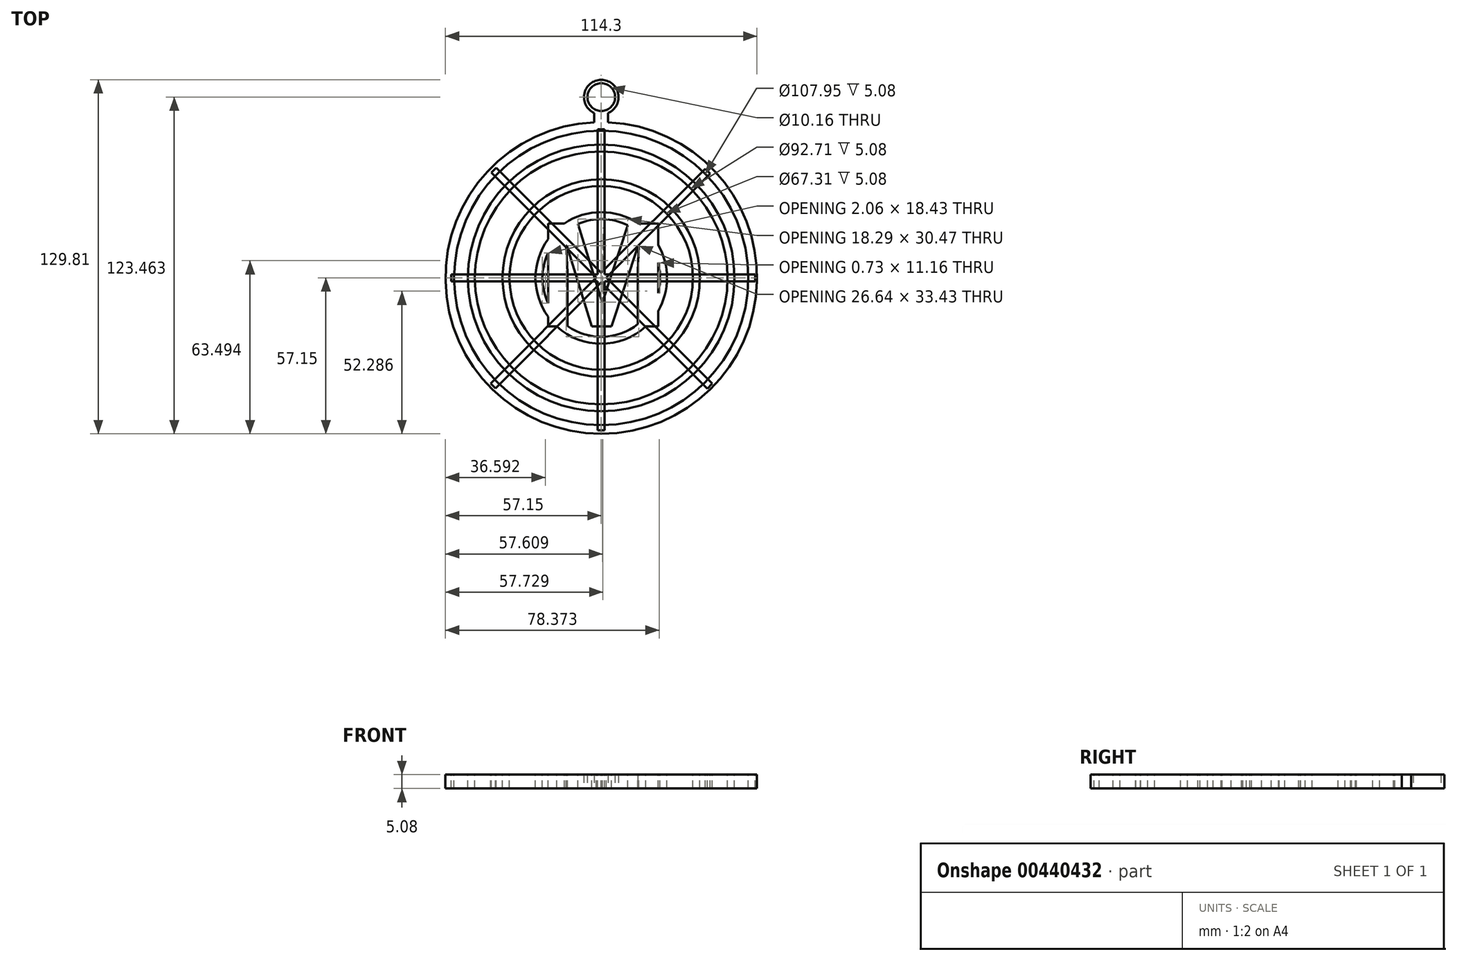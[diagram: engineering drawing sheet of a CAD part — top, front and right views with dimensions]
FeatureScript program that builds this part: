
annotation { "Feature Type Name" : "Feature", "Feature Type Description" : "" }
export const myFeature = defineFeature(function(context is Context, id is Id, definition is map)
    precondition{}
    {
        {
            var Q0;
            Q0=qCreatedBy(makeId("Top.planeOp"),FACE);
            var sketch = newSketch(context, id + "F0", { "sketchPlane" : qUnion([Q0])});
            skCircle(sketch, "E0", {"center": v(0, 0) * mm, "radius": 57.15 * mm});
            skSolve(sketch);
        }
        {
            var Q0;
            Q0 = qSketchRegion(id + "F0", true);
            extrude(context, id + "F1", {"entities" : qUnion([Q0]), "flatOperationType" : FlatOperationType.REMOVE, "offsetDistance" : 25.4 * mm, "depth" : 5.08 * mm, "domain" : OperationDomain.MODEL, "symmetric" : true});
        }
        {
            var Q0;
            Q0=makeQuery(id+"F1.opExtrude","CAP_FACE",FACE,{"disambiguationData":[OSD([sQuery(id+"F0.wireOp",EDGE,"E0")])],"isStart":false});
            var sketch = newSketch(context, id + "F2", { "sketchPlane" : qUnion([Q0])});
            skCircle(sketch, "E1", {"center": v(0, 0) * mm, "radius": 53.97 * mm});
            skText(sketch, "E2", { "text": "M", "fontName": "OpenSans-Bold.ttf"});
            skCircle(sketch, "E3", {"center": v(0, 0) * mm, "radius": 48.9 * mm});
            skCircle(sketch, "E4", {"center": v(0, 0) * mm, "radius": 46.35 * mm});
            skCircle(sketch, "E5", {"center": v(0, 0) * mm, "radius": 36.2 * mm});
            skCircle(sketch, "E6", {"center": v(0, 0) * mm, "radius": 33.66 * mm});
            skCircle(sketch, "E7", {"center": v(0, 0) * mm, "radius": 21.59 * mm});
            skCircle(sketch, "E8", {"center": v(0, 0) * mm, "radius": 24.13 * mm});
            const initialGuessF2  = {"E2": [-0.02428, -0.01778, 1, 0, 0.0381]};
            skSetInitialGuess(sketch, initialGuessF2);
            skSolve(sketch);
        }
        {
            var Q0;
            Q0=makeQuery(id+"F2.imprint","IMPRINT",FACE,{"disambiguationData":[TD([[makeQuery(id+"F2.imprint","IMPRINT",EDGE,{"derivedFrom":sQuery(id+"F2.wireOp",EDGE,"E2.sketch_text.stroke-0")}),1.0]])]});
            var Q1;
            Q1=makeQuery(id+"F2.imprint","IMPRINT",FACE,{"disambiguationData":[TD([[makeQuery(id+"F2.imprint","IMPRINT",EDGE,{"derivedFrom":sQuery(id+"F2.wireOp",EDGE,"E4")}),1.0]])]});
            var Q2;
            Q2=makeQuery(id+"F2.imprint","IMPRINT",FACE,{"disambiguationData":[TD([[makeQuery(id+"F2.imprint","IMPRINT",EDGE,{"derivedFrom":sQuery(id+"F2.wireOp",EDGE,"E1")}),1.0]])]});
            var Q3;
            Q3=makeQuery(id+"F2.imprint","IMPRINT",FACE,{"disambiguationData":[TD([[makeQuery(id+"F2.imprint","IMPRINT",EDGE,{"derivedFrom":sQuery(id+"F2.wireOp",EDGE,"E6")}),1.0]])]});
            var Q4;
            {var subQ0=sQuery(id+"F2.wireOp",EDGE,"E7");var subQ1=sQuery(id+"F2.wireOp",EDGE,"E2.sketch_text.stroke-5");var subQ2=makeQuery(id+"F2.imprint","INTERSECT",VERTEX,{"disambiguationData":[OD(0.0)],"derivedFrom":[subQ1,subQ0]});Q4=makeQuery(id+"F2.imprint","IMPRINT",FACE,{"disambiguationData":[TD([[makeQuery(id+"F2.imprint","IMPRINT",EDGE,{"disambiguationData":[TD([[subQ2,-1.0]])],"derivedFrom":subQ1}),1.0]])]});}
            var Q5;
            {var subQ0=sQuery(id+"F2.wireOp",EDGE,"E2.sketch_text.stroke-8");Q5=makeQuery(id+"F2.imprint","IMPRINT",FACE,{"disambiguationData":[TD([[makeQuery(id+"F2.imprint","IMPRINT",EDGE,{"derivedFrom":subQ0}),1.0]])]});}
            var Q6;
            {var subQ0=sQuery(id+"F2.wireOp",EDGE,"E7");var subQ1=sQuery(id+"F2.wireOp",EDGE,"E2.sketch_text.stroke-11");var subQ2=makeQuery(id+"F2.imprint","INTERSECT",VERTEX,{"disambiguationData":[OD(0.0)],"derivedFrom":[subQ1,subQ0]});Q6=makeQuery(id+"F2.imprint","IMPRINT",FACE,{"disambiguationData":[TD([[makeQuery(id+"F2.imprint","IMPRINT",EDGE,{"disambiguationData":[TD([[subQ2,-1.0]])],"derivedFrom":subQ1}),1.0]])]});}
            var Q7;
            Q7=makeQuery(id+"F1.opExtrude","CAP_FACE",FACE,{"disambiguationData":[OSD([sQuery(id+"F0.wireOp",EDGE,"E0")])],"isStart":true});
            extrude(context, id + "F3", {"entities" : qUnion([Q0, Q1, Q2, Q3, Q4, Q5, Q6]), "operationType" : NewBodyOperationType.REMOVE, "endBound" : BoundingType.UP_TO_SURFACE, "oppositeDirection" : true, "endBoundEntityFace" : qUnion([Q7]), "depth" : 25.4 * mm});
        }
        {
            var Q0;
            Q0=makeQuery(id+"F3.boolean.opBoolean","SPLIT",FACE,{"disambiguationData":[TD([makeQuery(id+"F3.opExtrude","SWEPT_FACE",FACE,{"disambiguationData":[OSD([sQuery(id+"F2.wireOp",EDGE,"E2.sketch_text.stroke-0")])]})])],"derivedFrom":makeQuery(id+"F1.opExtrude","CAP_FACE",FACE,{"disambiguationData":[OSD([sQuery(id+"F0.wireOp",EDGE,"E0")])],"isStart":false})});
            var sketch = newSketch(context, id + "F4", { "sketchPlane" : qUnion([Q0])});
            skLineSegment(sketch, "E9.bottom", {"start": v(-1.27, -17.78) * mm, "end": v(1.27, -17.78) * mm});
            skLineSegment(sketch, "E9.top", {"start": v(-1.27, -55.88) * mm, "end": v(1.27, -55.88) * mm});
            skLineSegment(sketch, "E9.left", {"start": v(-1.27, -17.78) * mm, "end": v(-1.27, -55.88) * mm});
            skLineSegment(sketch, "E9.right", {"start": v(1.27, -17.78) * mm, "end": v(1.27, -55.88) * mm});
            skLineSegment(sketch, "E10.top", {"start": v(-1.27, 54.5) * mm, "end": v(1.27, 54.5) * mm});
            skLineSegment(sketch, "E10.left", {"start": v(-1.27, -3.77) * mm, "end": v(-1.27, 54.5) * mm});
            skLineSegment(sketch, "E10.right", {"start": v(1.27, -6.46) * mm, "end": v(1.27, 54.5) * mm});
            skLineSegment(sketch, "E11.bottom", {"start": v(20.85, 1.27) * mm, "end": v(56.41, 1.27) * mm});
            skLineSegment(sketch, "E11.top", {"start": v(20.85, -1.27) * mm, "end": v(56.41, -1.27) * mm});
            skLineSegment(sketch, "E11.left", {"start": v(20.85, 1.27) * mm, "end": v(20.85, -1.27) * mm});
            skLineSegment(sketch, "E11.right", {"start": v(56.41, 1.27) * mm, "end": v(56.41, -1.27) * mm});
            skLineSegment(sketch, "E12.bottom", {"start": v(-19.53, 1.27) * mm, "end": v(-55.09, 1.27) * mm});
            skLineSegment(sketch, "E12.top", {"start": v(-19.53, -1.27) * mm, "end": v(-55.09, -1.27) * mm});
            skLineSegment(sketch, "E12.left", {"start": v(-19.53, 1.27) * mm, "end": v(-19.53, -1.27) * mm});
            skLineSegment(sketch, "E12.right", {"start": v(-55.09, 1.27) * mm, "end": v(-55.09, -1.27) * mm});
            skLineSegment(sketch, "E13.bottom", {"start": v(-19.53, 1.27) * mm, "end": v(20.85, 1.27) * mm});
            skLineSegment(sketch, "E13.top", {"start": v(-19.53, -1.27) * mm, "end": v(20.85, -1.27) * mm});
            skLineSegment(sketch, "E14.bottom", {"start": v(-1.27, -3.77) * mm, "end": v(1.27, -3.77) * mm});
            skLineSegment(sketch, "E14.left", {"start": v(-1.27, -3.77) * mm, "end": v(-1.27, -17.78) * mm});
            skLineSegment(sketch, "E14.right", {"start": v(1.27, -3.77) * mm, "end": v(1.27, -17.78) * mm});
            skSolve(sketch);
        }
        {
            var Q0;
            Q0 = qSketchRegion(id + "F4", true);
            var Q1;
            {var subQ0=sQuery(id+"F0.wireOp",EDGE,"E0");Q1=makeQuery(id+"F3.boolean.opBoolean","SPLIT",FACE,{"disambiguationData":[TD([makeQuery(id+"F1.opExtrude","SWEPT_FACE",FACE,{"disambiguationData":[OSD([subQ0])]})])],"derivedFrom":makeQuery(id+"F1.opExtrude","CAP_FACE",FACE,{"disambiguationData":[OSD([subQ0])],"isStart":true})});}
            extrude(context, id + "F5", {"entities" : qUnion([Q0]), "endBound" : BoundingType.UP_TO_SURFACE, "oppositeDirection" : true, "endBoundEntityFace" : qUnion([Q1]), "depth" : 25.4 * mm});
        }
        {
            var Q0;
            Q0=makeQuery(id+"F3.boolean.opBoolean","SPLIT",FACE,{"disambiguationData":[TD([makeQuery(id+"F3.opExtrude","SWEPT_FACE",FACE,{"disambiguationData":[OSD([sQuery(id+"F2.wireOp",EDGE,"E2.sketch_text.stroke-0")])]})])],"derivedFrom":makeQuery(id+"F1.opExtrude","CAP_FACE",FACE,{"disambiguationData":[OSD([sQuery(id+"F0.wireOp",EDGE,"E0")])],"isStart":false})});
            var sketch = newSketch(context, id + "F6", { "sketchPlane" : qUnion([Q0])});
            skLineSegment(sketch, "E15", {"start": v(0, 0.1) * mm, "end": v(-46.67, 46.77) * mm, "construction": true});
            skLineSegment(sketch, "E16", {"start": v(0, 0.1) * mm, "end": v(59.78, -59.67) * mm, "construction": true});
            skLineSegment(sketch, "E17", {"start": v(-40.32, 38.63) * mm, "end": v(38.89, -40.58) * mm});
            skLineSegment(sketch, "E18", {"start": v(38.89, -40.58) * mm, "end": v(40.68, -38.78) * mm});
            skLineSegment(sketch, "E19", {"start": v(40.68, -38.78) * mm, "end": v(-38.52, 40.42) * mm});
            skLineSegment(sketch, "E20", {"start": v(-40.32, 38.63) * mm, "end": v(-38.52, 40.42) * mm});
            skLineSegment(sketch, "E21", {"start": v(0, 0.1) * mm, "end": v(58.2, 58.3) * mm, "construction": true});
            skLineSegment(sketch, "E22", {"start": v(0, 0.1) * mm, "end": v(-51.68, -51.57) * mm, "construction": true});
            skLineSegment(sketch, "E23", {"start": v(38.11, 40.01) * mm, "end": v(-40.57, -38.67) * mm});
            skLineSegment(sketch, "E24", {"start": v(-40.57, -38.67) * mm, "end": v(-38.77, -40.46) * mm});
            skLineSegment(sketch, "E25", {"start": v(-38.77, -40.46) * mm, "end": v(39.91, 38.22) * mm});
            skLineSegment(sketch, "E26", {"start": v(38.11, 40.01) * mm, "end": v(39.91, 38.22) * mm});
            skSolve(sketch);
        }
        {
            var Q0;
            Q0 = qSketchRegion(id + "F6", true);
            var Q1;
            {var subQ0=sQuery(id+"F0.wireOp",EDGE,"E0");Q1=makeQuery(id+"F3.boolean.opBoolean","SPLIT",FACE,{"disambiguationData":[TD([makeQuery(id+"F1.opExtrude","SWEPT_FACE",FACE,{"disambiguationData":[OSD([subQ0])]})])],"derivedFrom":makeQuery(id+"F1.opExtrude","CAP_FACE",FACE,{"disambiguationData":[OSD([subQ0])],"isStart":true})});}
            extrude(context, id + "F7", {"entities" : qUnion([Q0]), "endBound" : BoundingType.UP_TO_SURFACE, "oppositeDirection" : true, "endBoundEntityFace" : qUnion([Q1]), "depth" : 25.4 * mm});
        }
        {
            var Q0;
            Q0=qCreatedBy(makeId("Top.planeOp"),FACE);
            var sketch = newSketch(context, id + "F8", { "sketchPlane" : qUnion([Q0])});
            skLineSegment(sketch, "E27.bottom", {"start": v(-2.54, 55.88) * mm, "end": v(2.54, 55.88) * mm});
            skLineSegment(sketch, "E27.left", {"start": v(-2.54, 55.88) * mm, "end": v(-2.54, 60.5) * mm});
            skLineSegment(sketch, "E27.right", {"start": v(2.54, 55.88) * mm, "end": v(2.54, 60.5) * mm});
            skArc(sketch, "E28", {"start": v(2.54, 60.5) * mm, "mid": v(0, 72.66) * mm, "end": v(-2.54, 60.5) * mm});
            skCircle(sketch, "E29", {"center": v(0, 66.31) * mm, "radius": 5.08 * mm});
            skSolve(sketch);
        }
        {
            var Q0;
            Q0 = qSketchRegion(id + "F8", true);
            extrude(context, id + "F9", {"entities" : qUnion([Q0]), "operationType" : NewBodyOperationType.ADD, "depth" : 5.08 * mm, "symmetric" : true});
        }
    });
